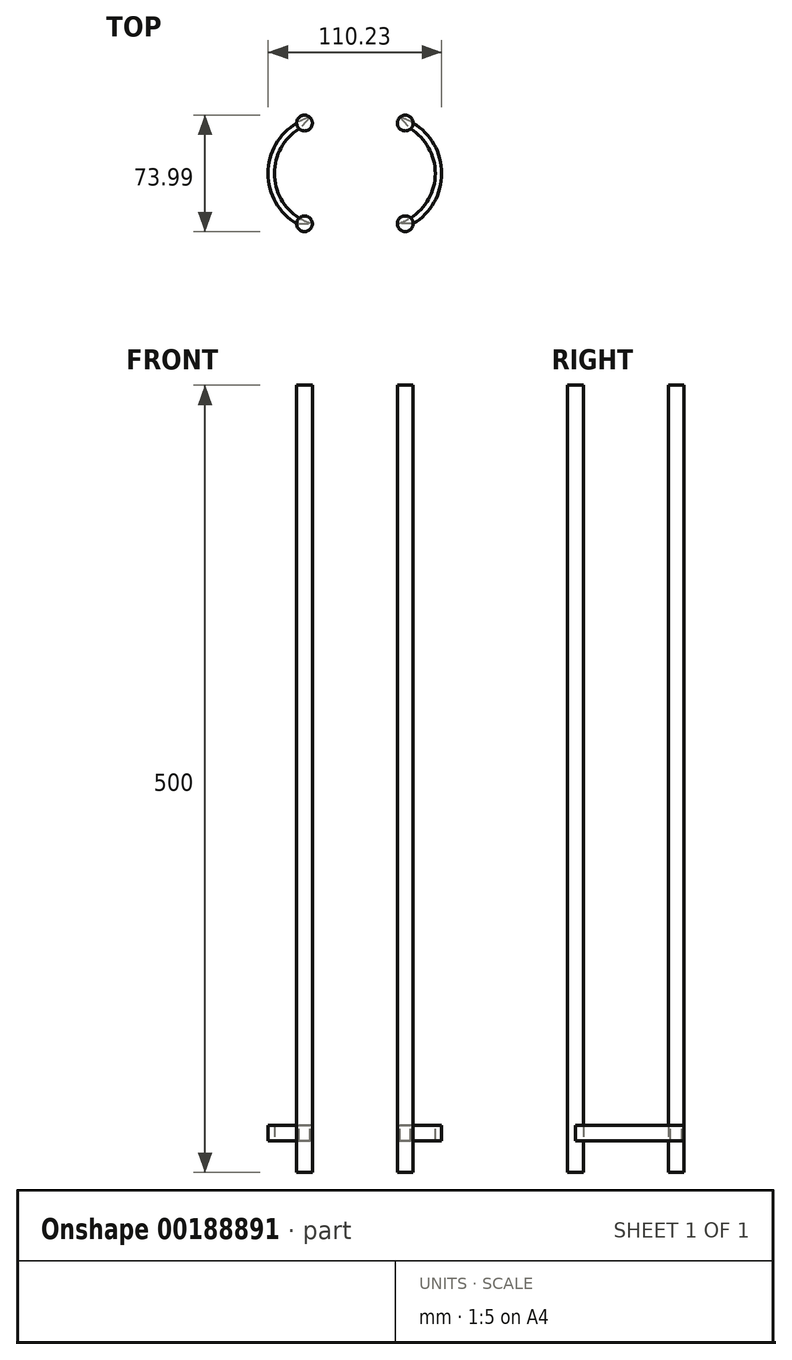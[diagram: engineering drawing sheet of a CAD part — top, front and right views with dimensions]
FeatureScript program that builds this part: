
annotation { "Feature Type Name" : "Feature", "Feature Type Description" : "" }
export const myFeature = defineFeature(function(context is Context, id is Id, definition is map)
    precondition{}
    {
        {
            var Q0;
            Q0=qCreatedBy(makeId("Top.planeOp"),FACE);
            var sketch = newSketch(context, id + "F0", { "sketchPlane" : qUnion([Q0])});
            skCircle(sketch, "E0", {"center": v(0, 0) * mm, "radius": 40 * mm});
            skSolve(sketch);
        }
        {
            var Q0;
            Q0=qCreatedBy(makeId("Top.planeOp"),FACE);
            var sketch = newSketch(context, id + "F1", { "sketchPlane" : qUnion([Q0])});
            skCircle(sketch, "E1", {"center": v(-31.82, -31.82) * mm, "radius": 5 * mm});
            skCircle(sketch, "E2.1.0", {"center": v(-31.82, 32.17) * mm, "radius": 5 * mm});
            skCircle(sketch, "E2.2.0", {"center": v(32.17, 32.17) * mm, "radius": 5 * mm});
            skCircle(sketch, "E2.3.0", {"center": v(32.17, -31.82) * mm, "radius": 5 * mm});
            skPoint(sketch, "E2.center", {"position": v(0.18, 0.18) * mm});
            skLineSegment(sketch, "E2.anchor1", {"start": v(0.18, 0.18) * mm, "end": v(-31.82, -31.82) * mm, "construction": true});
            skLineSegment(sketch, "E2.anchor2", {"start": v(0.18, 0.18) * mm, "end": v(32.17, -31.82) * mm, "construction": true});
            skSolve(sketch);
        }
        {
            var Q0;
            Q0=qSketchRegion(id+"F1",true);
            extrude(context, id + "F2", {"entities" : qUnion([Q0]), "depth" : 500 * mm});
        }
        {
            var Q0;
            Q0=qCreatedBy(makeId("Top.planeOp"),FACE);
            cPlane(context, id + "F3", {"entities" : qUnion([Q0]), "cplaneType" : CPlaneType.OFFSET, "offset" : 25 * mm, "width" : 150 * mm, "height" : 150 * mm});
        }
        {
            var Q0;
            Q0=qCreatedBy(id+"F3.planeOp",FACE);
            var sketch = newSketch(context, id + "F4", { "sketchPlane" : qUnion([Q0])});
            skArc(sketch, "E3", {"start": v(-31.82, 32.17) * mm, "mid": v(-52.63, 0.18) * mm, "end": v(-31.82, -31.82) * mm});
            skArc(sketch, "E4", {"start": v(32.17, -31.82) * mm, "mid": v(52.99, 0.18) * mm, "end": v(32.17, 32.17) * mm});
            skSolve(sketch);
        }
        {
            var Q0;
            Q0=qCreatedBy(makeId("Front.planeOp"),FACE);
            var Q1;
            Q1=sQuery(id+"F4.wireOp",VERTEX,"E3.end");
            cPlane(context, id + "F5", {"entities" : qUnion([Q0, Q1]), "cplaneType" : CPlaneType.PLANE_POINT, "offset" : 35 * mm, "width" : 150 * mm, "height" : 150 * mm});
        }
        {
            var Q0;
            Q0=qCreatedBy(id+"F5.planeOp",FACE);
            var sketch = newSketch(context, id + "F6", { "sketchPlane" : qUnion([Q0])});
            skLineSegment(sketch, "E5.bottom", {"start": v(-36.82, 20) * mm, "end": v(-26.82, 20) * mm});
            skLineSegment(sketch, "E5.top", {"start": v(-36.82, 30) * mm, "end": v(-26.82, 30) * mm});
            skLineSegment(sketch, "E5.left", {"start": v(-36.82, 20) * mm, "end": v(-36.82, 30) * mm});
            skLineSegment(sketch, "E5.right", {"start": v(-26.82, 20) * mm, "end": v(-26.82, 30) * mm});
            skPoint(sketch, "E5.middle", {"position": v(-31.82, 25) * mm});
            skSolve(sketch);
        }
        {
            var Q0;
            Q0=qSketchRegion(id+"F6",true);
            var Q1;
            Q1=sQuery(id+"F4.wireOp",EDGE,"E3");
            sweep(context, id + "F7", {"profiles" : qUnion([Q0]), "path" : qUnion([Q1])});
        }
        {
            var Q0;
            Q0=qCreatedBy(id+"F5.planeOp",FACE);
            var sketch = newSketch(context, id + "F8", { "sketchPlane" : qUnion([Q0])});
            skLineSegment(sketch, "E6.bottom", {"start": v(37.17, 20) * mm, "end": v(27.17, 20) * mm});
            skLineSegment(sketch, "E6.top", {"start": v(37.17, 30) * mm, "end": v(27.17, 30) * mm});
            skLineSegment(sketch, "E6.left", {"start": v(37.17, 20) * mm, "end": v(37.17, 30) * mm});
            skLineSegment(sketch, "E6.right", {"start": v(27.17, 20) * mm, "end": v(27.17, 30) * mm});
            skPoint(sketch, "E6.middle", {"position": v(32.17, 25) * mm});
            skSolve(sketch);
        }
        {
            var Q0;
            Q0=qSketchRegion(id+"F8",true);
            var Q1;
            Q1=sQuery(id+"F4.wireOp",EDGE,"E4");
            sweep(context, id + "F9", {"profiles" : qUnion([Q0]), "path" : qUnion([Q1])});
        }
    });
